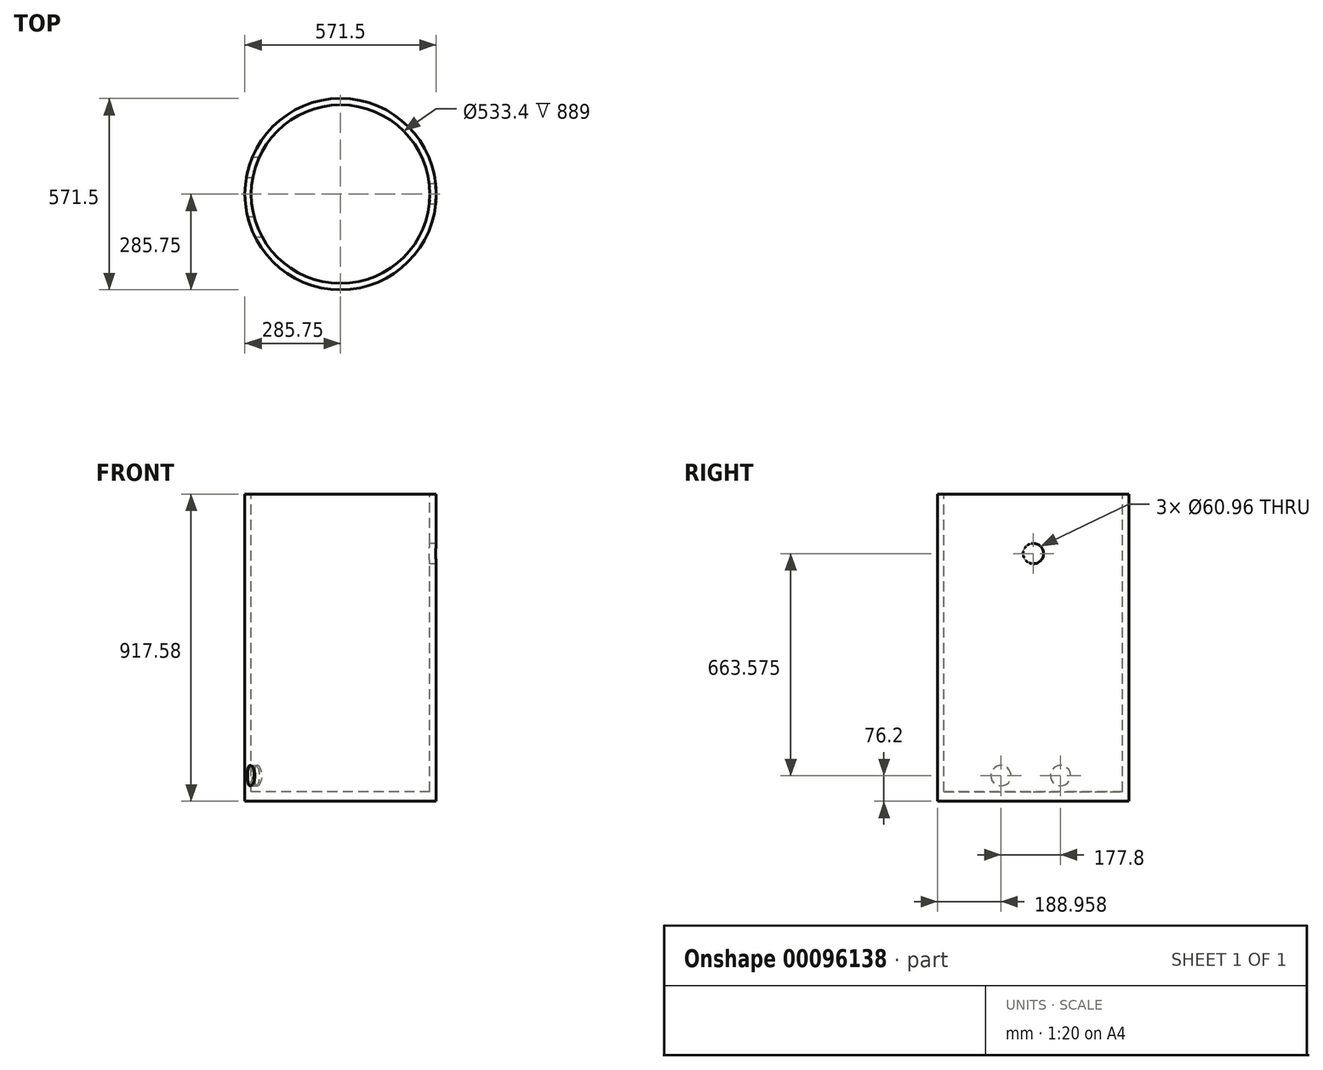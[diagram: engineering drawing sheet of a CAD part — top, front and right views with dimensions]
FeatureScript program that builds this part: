
annotation { "Feature Type Name" : "Feature", "Feature Type Description" : "" }
export const myFeature = defineFeature(function(context is Context, id is Id, definition is map)
    precondition{}
    {
        {
            var Q0;
            Q0=qCreatedBy(makeId("Top.planeOp"),FACE);
            var sketch = newSketch(context, id + "F0", { "sketchPlane" : qUnion([Q0])});
            skCircle(sketch, "E0", {"center": v(0, 0) * mm, "radius": 285.75 * mm});
            skSolve(sketch);
        }
        {
            var Q0;
            Q0=makeQuery(id+"F0.imprint","IMPRINT",FACE,{"disambiguationData":[TD([[makeQuery(id+"F0.imprint","IMPRINT",EDGE,{"derivedFrom":sQuery(id+"F0.wireOp",EDGE,"E0")}),1.0]])]});
            extrude(context, id + "F1", {"entities" : qUnion([Q0]), "depth" : 917.57 * mm});
        }
        {
            var Q0;
            Q0=makeQuery(id+"F1.opExtrude","CAP_FACE",FACE,{"disambiguationData":[OSD([sQuery(id+"F0.wireOp",EDGE,"E0")])],"isStart":false});
            var sketch = newSketch(context, id + "F2", { "sketchPlane" : qUnion([Q0])});
            skCircle(sketch, "E1", {"center": v(0, 0) * mm, "radius": 266.7 * mm});
            skSolve(sketch);
        }
        {
            var Q0;
            Q0=makeQuery(id+"F2.imprint","IMPRINT",FACE,{"disambiguationData":[TD([[makeQuery(id+"F2.imprint","IMPRINT",EDGE,{"derivedFrom":sQuery(id+"F2.wireOp",EDGE,"E1")}),1.0]])]});
            var Q1;
            Q1=sQuery(id+"F2.wireOp",EDGE,"E1");
            extrude(context, id + "F3", {"entities" : qUnion([Q0]), "operationType" : NewBodyOperationType.REMOVE, "surfaceEntities" : qUnion([Q1]), "oppositeDirection" : true, "depth" : 889 * mm});
        }
        {
            var Q0;
            Q0=qCreatedBy(makeId("Right.planeOp"),FACE);
            var sketch = newSketch(context, id + "F4", { "sketchPlane" : qUnion([Q0])});
            skCircle(sketch, "E2", {"center": v(0, 739.78) * mm, "radius": 30.48 * mm});
            skSolve(sketch);
        }
        {
            var Q0;
            Q0=qSketchRegion(id+"F4",true);
            extrude(context, id + "F5", {"entities" : qUnion([Q0]), "operationType" : NewBodyOperationType.REMOVE, "depth" : 547.83 * mm});
        }
        {
            var Q0;
            Q0=qCreatedBy(makeId("Right.planeOp"),FACE);
            var sketch = newSketch(context, id + "F6", { "sketchPlane" : qUnion([Q0])});
            skCircle(sketch, "E3", {"center": v(81, 76.2) * mm, "radius": 30.48 * mm});
            skCircle(sketch, "E4", {"center": v(-96.8, 76.2) * mm, "radius": 30.48 * mm});
            skSolve(sketch);
        }
        {
            var Q0;
            Q0=qSketchRegion(id+"F6",true);
            extrude(context, id + "F7", {"entities" : qUnion([Q0]), "operationType" : NewBodyOperationType.REMOVE, "oppositeDirection" : true, "depth" : 651.82 * mm});
        }
    });
